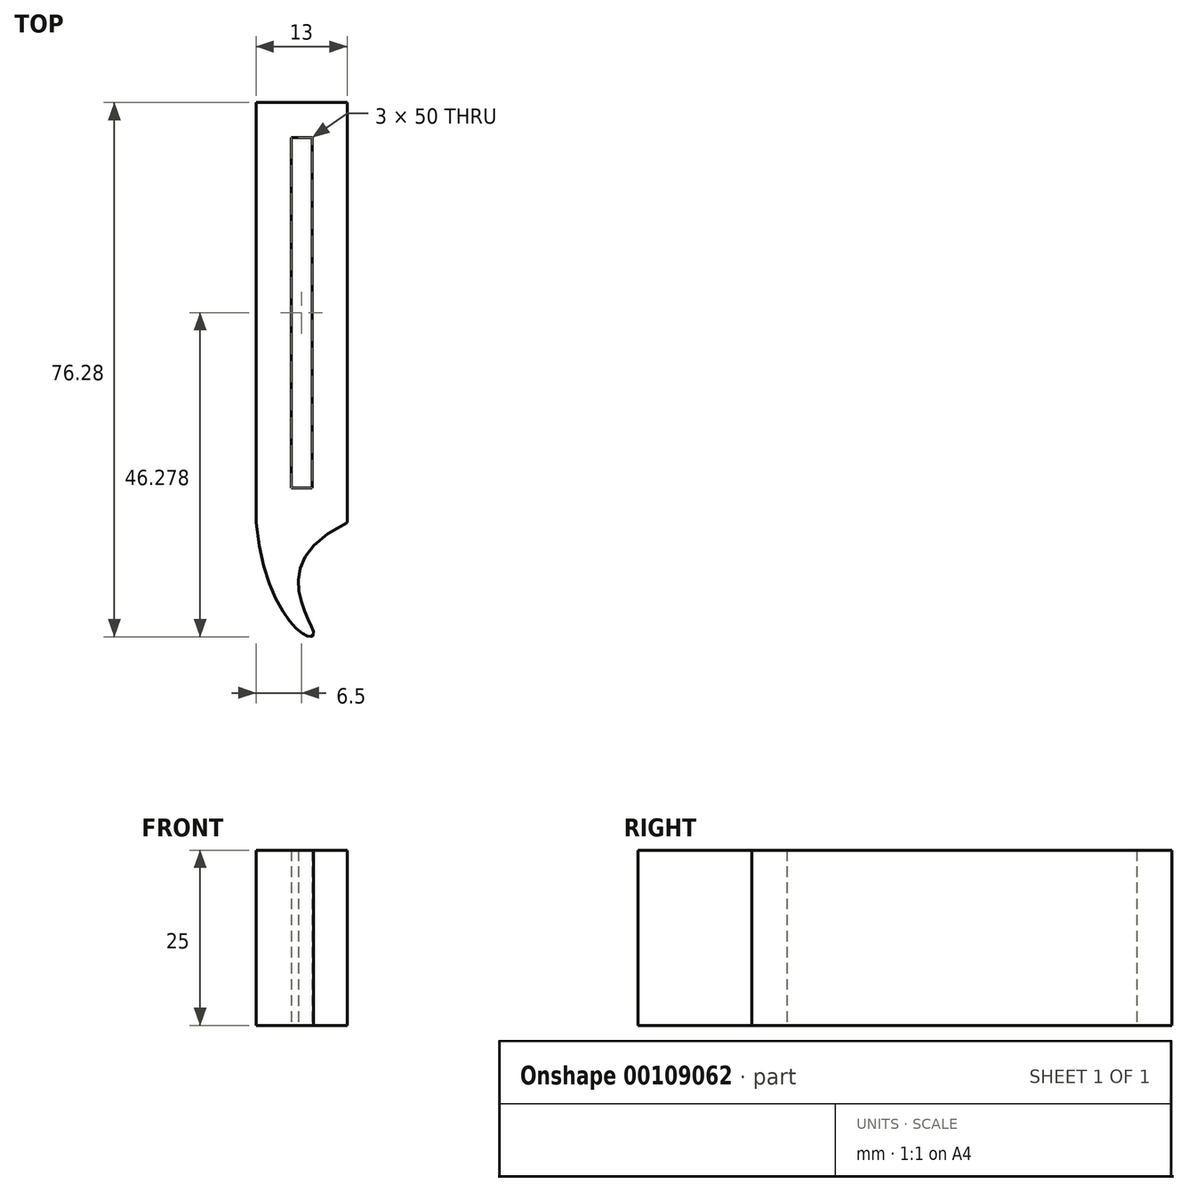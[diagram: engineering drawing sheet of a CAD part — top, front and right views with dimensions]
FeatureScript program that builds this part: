
annotation { "Feature Type Name" : "Feature", "Feature Type Description" : "" }
export const myFeature = defineFeature(function(context is Context, id is Id, definition is map)
    precondition{}
    {
        {
            var Q0;
            Q0=qCreatedBy(makeId("Top.planeOp"),FACE);
            var sketch = newSketch(context, id + "F0", { "sketchPlane" : qUnion([Q0])});
            skLineSegment(sketch, "E0.bottom", {"start": v(0, 29.5) * mm, "end": v(3, 29.5) * mm});
            skLineSegment(sketch, "E0.top", {"start": v(0, -20.5) * mm, "end": v(3, -20.5) * mm});
            skLineSegment(sketch, "E0.left", {"start": v(0, 29.5) * mm, "end": v(0, -20.5) * mm});
            skLineSegment(sketch, "E0.right", {"start": v(3, 29.5) * mm, "end": v(3, -20.5) * mm});
            skLineSegment(sketch, "E1.0", {"start": v(-5, 34.5) * mm, "end": v(8, 34.5) * mm});
            skLineSegment(sketch, "E1.1", {"start": v(-5, 34.5) * mm, "end": v(-5, -25.5) * mm});
            skLineSegment(sketch, "E1.2", {"start": v(-5, -25.5) * mm, "end": v(8, -25.5) * mm});
            skLineSegment(sketch, "E1.3", {"start": v(8, 34.5) * mm, "end": v(8, -25.5) * mm});
            skFitSpline(sketch, "E2", {"points": [v(-5, -25.5) * mm, v(3.2, -41.24) * mm, v(8, -25.5) * mm], "startDerivative": vector(7.53, -81.08) * mm, "endDerivative": vector(72.95, 34.91) * mm});
            skSolve(sketch);
        }
        {
            var Q0;
            Q0=makeQuery(id+"F0.imprint","IMPRINT",FACE,{"disambiguationData":[TD([[makeQuery(id+"F0.imprint","IMPRINT",EDGE,{"derivedFrom":sQuery(id+"F0.wireOp",EDGE,"E1.2")}),-1.0]])]});
            var Q1;
            Q1=makeQuery(id+"F0.imprint","IMPRINT",FACE,{"disambiguationData":[TD([[makeQuery(id+"F0.imprint","IMPRINT",EDGE,{"derivedFrom":sQuery(id+"F0.wireOp",EDGE,"E0.bottom")}),1.0]])]});
            extrude(context, id + "F1", {"entities" : qUnion([Q0, Q1]), "depth" : 25 * mm});
        }
    });
